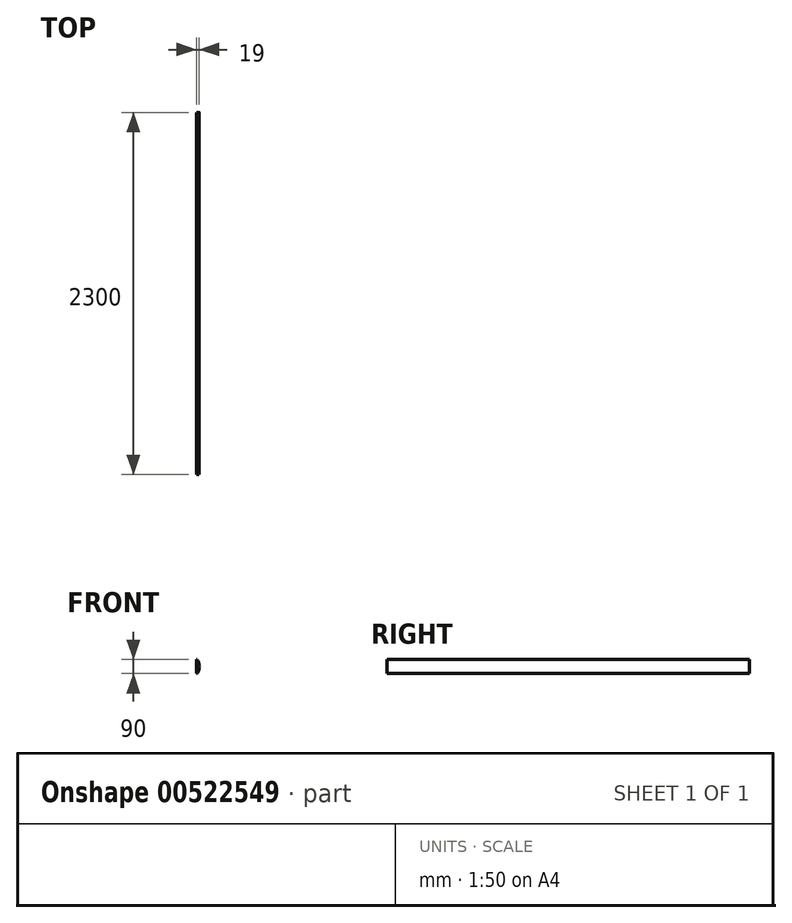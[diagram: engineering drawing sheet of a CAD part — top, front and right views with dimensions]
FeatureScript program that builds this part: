
annotation { "Feature Type Name" : "Feature", "Feature Type Description" : "" }
export const myFeature = defineFeature(function(context is Context, id is Id, definition is map)
    precondition{}
    {
        {
            var Q0;
            Q0=qCreatedBy(makeId("Front.planeOp"),FACE);
            var sketch = newSketch(context, id + "F0", { "sketchPlane" : qUnion([Q0])});
            skLineSegment(sketch, "E0", {"start": v(0, 0) * mm, "end": v(0, 90) * mm});
            skLineSegment(sketch, "E1", {"start": v(0, 0) * mm, "end": v(5, 0) * mm});
            skLineSegment(sketch, "E2", {"start": v(0, 90) * mm, "end": v(5, 90) * mm});
            skLineSegment(sketch, "E3", {"start": v(0, 45) * mm, "end": v(19, 45) * mm});
            skPoint(sketch, "E3.endSnap0", {"position": v(0, 45) * mm});
            skArc(sketch, "E4", {"start": v(5, 0) * mm, "mid": v(19, 45) * mm, "end": v(5, 90) * mm});
            skSolve(sketch);
        }
        {
            var Q0;
            Q0 = qSketchRegion(id + "F0", true);
            extrude(context, id + "F1", {"entities" : qUnion([Q0]), "depth" : 2300 * mm, "offsetDistance" : 25 * mm});
        }
    });
